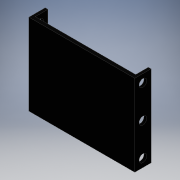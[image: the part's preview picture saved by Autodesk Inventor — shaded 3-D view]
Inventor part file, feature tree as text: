
AUTODESK INVENTOR PART (.ipt)
format: ipt  version: 2016 (Build 200138000, 138)  size: 119,296 bytes
history: native  units: mm
features: sketch x3, extrude x2, hole x1
ambient origin geometry x8: Origin, YZ Plane, XZ Plane, XY Plane, X Axis, Y Axis, Z Axis, Center Point
bodies: Solid1 (feature_tree)
feature tree (6):
  extrude  "Extrusion1"  Depth=45.0mm
  extrude  "Extrusion2"  Depth=1.5mm
  hole  "Hole1"  [1 undecoded]
  sketch  "Sketch1"  dims[d0=55.5mm d1=45.0mm]
  sketch  "Sketch2"  dims[d2=2.0mm d3=0.0mm d4=1.5mm]
  sketch  "Sketch3"  dims[d5=1.5mm d6=9.0mm d7=0.0mm d8=4.3mm d9=4.5mm d10=4.5mm d11=4.3mm d12=4.5mm d13=4.5mm d14=4.3mm d15=4.3mm d16=6.0mm d17=4.0mm d18=2.0mm d19=90.0deg d20=8.0mm d21=20.594885mm]
note: 1 required parameter value undecoded (feature->parameter linkage not recoverable at this tier; creation-order binding heuristic only, values carry confidence <= 0.55)
